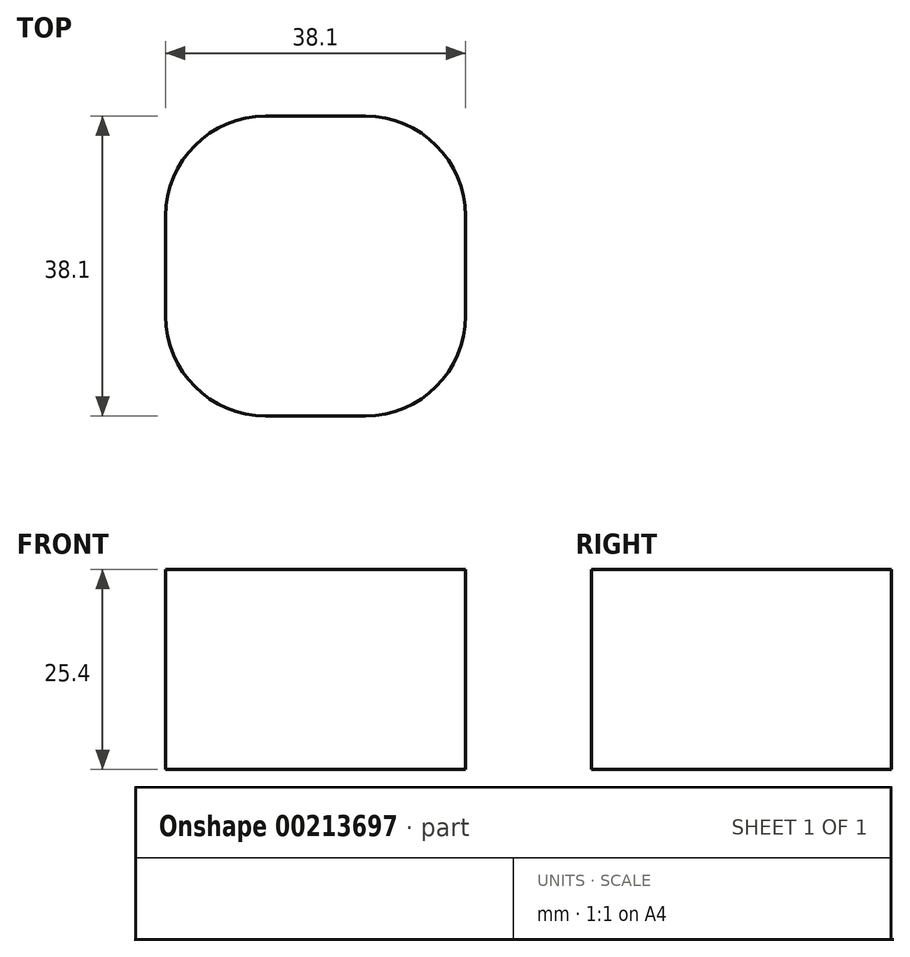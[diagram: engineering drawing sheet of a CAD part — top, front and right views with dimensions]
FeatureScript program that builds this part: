
annotation { "Feature Type Name" : "Feature", "Feature Type Description" : "" }
export const myFeature = defineFeature(function(context is Context, id is Id, definition is map)
    precondition{}
    {
        {
            var Q0;
            Q0=qCreatedBy(makeId("Top.planeOp"),FACE);
            var sketch = newSketch(context, id + "F0", { "sketchPlane" : qUnion([Q0])});
            skLineSegment(sketch, "E0.bottom", {"start": v(19.05, 19.05) * mm, "end": v(-19.05, 19.05) * mm});
            skLineSegment(sketch, "E0.top", {"start": v(19.05, -19.05) * mm, "end": v(-19.05, -19.05) * mm});
            skLineSegment(sketch, "E0.left", {"start": v(31.75, 6.35) * mm, "end": v(31.75, -6.35) * mm});
            skLineSegment(sketch, "E0.right", {"start": v(-31.75, 6.35) * mm, "end": v(-31.75, -6.35) * mm});
            skPoint(sketch, "E0.middle", {"position": v(0, 0) * mm});
            skPoint(sketch, "E1.visualSharp", {"position": v(-31.75, 19.05) * mm});
            skArc(sketch, "E1.filletArc", {"start": v(-19.05, 19.05) * mm, "mid": v(-28.03, 15.33) * mm, "end": v(-31.75, 6.35) * mm});
            skPoint(sketch, "E2.visualSharp", {"position": v(-31.75, -19.05) * mm});
            skArc(sketch, "E2.filletArc", {"start": v(-31.75, -6.35) * mm, "mid": v(-28.03, -15.33) * mm, "end": v(-19.05, -19.05) * mm});
            skPoint(sketch, "E3.visualSharp", {"position": v(31.75, 19.05) * mm});
            skArc(sketch, "E3.filletArc", {"start": v(31.75, 6.35) * mm, "mid": v(28.03, 15.33) * mm, "end": v(19.05, 19.05) * mm});
            skPoint(sketch, "E4.visualSharp", {"position": v(31.75, -19.05) * mm});
            skArc(sketch, "E4.filletArc", {"start": v(19.05, -19.05) * mm, "mid": v(28.03, -15.33) * mm, "end": v(31.75, -6.35) * mm});
            skSolve(sketch);
        }
        {
            var Q0;
            Q0=makeQuery(id+"F0.imprint","IMPRINT",FACE,{"disambiguationData":[TD([[makeQuery(id+"F0.imprint","IMPRINT",EDGE,{"derivedFrom":sQuery(id+"F0.wireOp",EDGE,"E0.bottom")}),1.0]])]});
            extrude(context, id + "F1", {"entities" : qUnion([Q0]), "depth" : 76.2 * mm});
        }
        {
            var Q0;
            Q0=makeQuery(id+"F1.opExtrude","CAP_FACE",FACE,{"disambiguationData":[OSD([sQuery(id+"F0.wireOp",EDGE,"E0.bottom"),sQuery(id+"F0.wireOp",EDGE,"E0.top"),sQuery(id+"F0.wireOp",EDGE,"E0.left"),sQuery(id+"F0.wireOp",EDGE,"E0.right"),sQuery(id+"F0.wireOp",EDGE,"E1.filletArc"),sQuery(id+"F0.wireOp",EDGE,"E2.filletArc"),sQuery(id+"F0.wireOp",EDGE,"E3.filletArc"),sQuery(id+"F0.wireOp",EDGE,"E4.filletArc")])],"isStart":false});
            extrude(context, id + "F2", {"entities" : qUnion([Q0]), "operationType" : NewBodyOperationType.REMOVE, "oppositeDirection" : true, "depth" : 25.4 * mm});
        }
        {
            var Q0;
            Q0=makeQuery(id+"F1.opExtrude","SWEPT_BODY",BODY,{"disambiguationData":[OSD([sQuery(id+"F0.wireOp",EDGE,"E0.bottom"),sQuery(id+"F0.wireOp",EDGE,"E0.top"),sQuery(id+"F0.wireOp",EDGE,"E0.left"),sQuery(id+"F0.wireOp",EDGE,"E0.right"),sQuery(id+"F0.wireOp",EDGE,"E1.filletArc"),sQuery(id+"F0.wireOp",EDGE,"E2.filletArc"),sQuery(id+"F0.wireOp",EDGE,"E3.filletArc"),sQuery(id+"F0.wireOp",EDGE,"E4.filletArc")])]});
            deleteBodies(context, id + "F3", {"entities" : qUnion([Q0])});
        }
        {
            var Q0;
            Q0=qCreatedBy(makeId("Top.planeOp"),FACE);
            var sketch = newSketch(context, id + "F4", { "sketchPlane" : qUnion([Q0])});
            skLineSegment(sketch, "E5.bottom", {"start": v(-6.35, 19.05) * mm, "end": v(6.35, 19.05) * mm});
            skLineSegment(sketch, "E5.top", {"start": v(-6.35, -19.05) * mm, "end": v(6.35, -19.05) * mm});
            skLineSegment(sketch, "E5.left", {"start": v(-19.05, 6.35) * mm, "end": v(-19.05, -6.35) * mm});
            skLineSegment(sketch, "E5.right", {"start": v(19.05, 6.35) * mm, "end": v(19.05, -6.35) * mm});
            skPoint(sketch, "E5.middle", {"position": v(0, 0) * mm});
            skPoint(sketch, "E6.visualSharp", {"position": v(-19.05, 19.05) * mm});
            skArc(sketch, "E6.filletArc", {"start": v(-6.35, 19.05) * mm, "mid": v(-15.33, 15.33) * mm, "end": v(-19.05, 6.35) * mm});
            skPoint(sketch, "E7.visualSharp", {"position": v(19.05, 19.05) * mm});
            skArc(sketch, "E7.filletArc", {"start": v(19.05, 6.35) * mm, "mid": v(15.33, 15.33) * mm, "end": v(6.35, 19.05) * mm});
            skPoint(sketch, "E8.visualSharp", {"position": v(19.05, -19.05) * mm});
            skArc(sketch, "E8.filletArc", {"start": v(6.35, -19.05) * mm, "mid": v(15.33, -15.33) * mm, "end": v(19.05, -6.35) * mm});
            skPoint(sketch, "E9.visualSharp", {"position": v(-19.05, -19.05) * mm});
            skArc(sketch, "E9.filletArc", {"start": v(-19.05, -6.35) * mm, "mid": v(-15.33, -15.33) * mm, "end": v(-6.35, -19.05) * mm});
            skSolve(sketch);
        }
        {
            var Q0;
            Q0=makeQuery(id+"F4.imprint","IMPRINT",FACE,{"disambiguationData":[TD([[makeQuery(id+"F4.imprint","IMPRINT",EDGE,{"derivedFrom":sQuery(id+"F4.wireOp",EDGE,"E5.bottom")}),-1.0]])]});
            extrude(context, id + "F5", {"entities" : qUnion([Q0]), "depth" : 50.8 * mm});
        }
        {
            var Q0;
            Q0=makeQuery(id+"F5.opExtrude","CAP_FACE",FACE,{"disambiguationData":[OSD([sQuery(id+"F4.wireOp",EDGE,"E5.bottom"),sQuery(id+"F4.wireOp",EDGE,"E5.top"),sQuery(id+"F4.wireOp",EDGE,"E5.left"),sQuery(id+"F4.wireOp",EDGE,"E5.right"),sQuery(id+"F4.wireOp",EDGE,"E6.filletArc"),sQuery(id+"F4.wireOp",EDGE,"E7.filletArc"),sQuery(id+"F4.wireOp",EDGE,"E8.filletArc"),sQuery(id+"F4.wireOp",EDGE,"E9.filletArc")])],"isStart":false});
            extrude(context, id + "F6", {"entities" : qUnion([Q0]), "operationType" : NewBodyOperationType.REMOVE, "oppositeDirection" : true, "depth" : 25.4 * mm});
        }
    });
